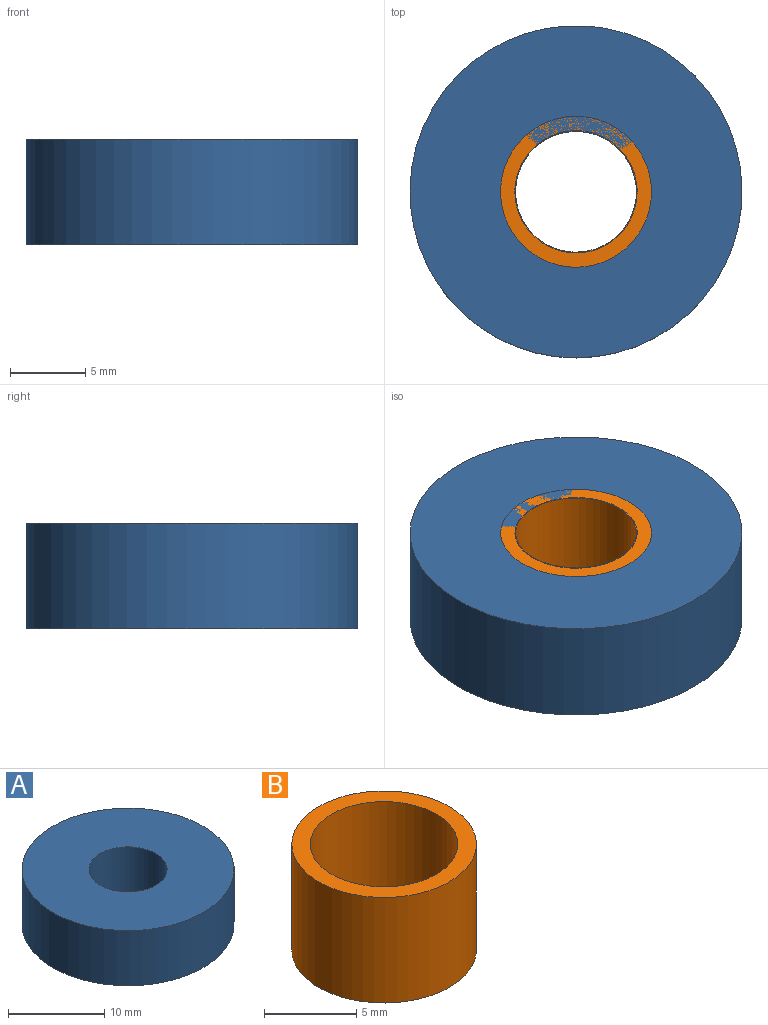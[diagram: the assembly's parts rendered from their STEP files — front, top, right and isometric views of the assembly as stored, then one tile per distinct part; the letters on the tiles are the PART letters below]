
ASSEMBLY  parts=2 mates=1
PART A: 4 faces, bbox 22x22x7 mm
  f0: cylinder r=4.05mm len=8.1mm, axis (0,0,-1), area 178.1mm2, adj f2,f3
  f1: cylinder r=11mm len=22mm, axis (0,0,-1), area 483.8mm2, adj f2,f3
  f2: plane 22x22mm, normal (0,0,1), area 328.6mm2, adj f0,f1
  f3: plane 22x22mm, normal (0,0,-1), area 328.6mm2, adj f0,f1
PART B: 4 faces, bbox 10x10x7 mm
  f0: cylinder r=4mm len=8mm, axis (0,0,-1), area 175.9mm2, adj f2,f3
  f1: cylinder r=5mm len=10mm, axis (0,0,-1), area 219.9mm2, adj f2,f3
  f2: plane 10x10mm, normal (0,0,1), area 28.3mm2, adj f0,f1
  f3: plane 10x10mm, normal (0,0,-1), area 28.3mm2, adj f0,f1
PLACE A rot(axis=(0,0,-1),89.9deg) t=(6.2,-0.69,13.86)mm
PLACE B t=(6.2,-0.69,13.86)mm fixed
MATE revolute A.f0 <-> B.f1  axis (0,0,-1) through (6.2,-0.69,13.86)mm
